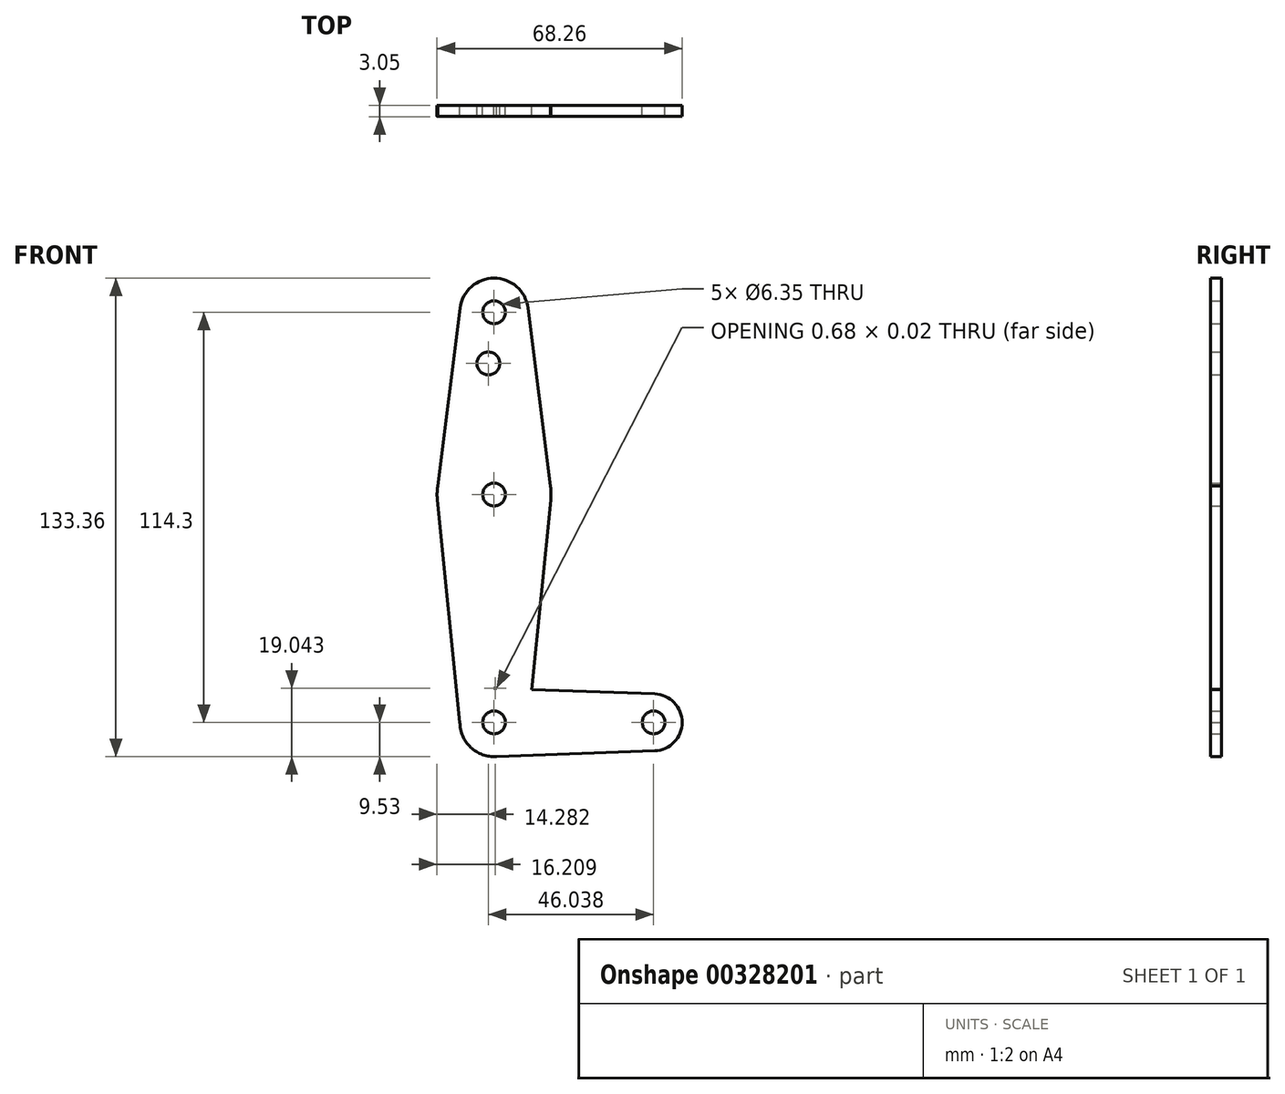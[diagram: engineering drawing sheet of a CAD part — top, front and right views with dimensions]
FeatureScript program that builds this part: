
annotation { "Feature Type Name" : "Feature", "Feature Type Description" : "" }
export const myFeature = defineFeature(function(context is Context, id is Id, definition is map)
    precondition{}
    {
        {
            var Q0;
            Q0=qCreatedBy(makeId("Front.planeOp"),FACE);
            var sketch = newSketch(context, id + "F0", { "sketchPlane" : qUnion([Q0])});
            skLineSegment(sketch, "E0", {"start": v(0, 0) * mm, "end": v(0, 114.3) * mm, "construction": true});
            skLineSegment(sketch, "E1", {"start": v(0, 0) * mm, "end": v(44.45, 0) * mm, "construction": true});
            skCircle(sketch, "E2", {"center": v(0, 114.3) * mm, "radius": 9.53 * mm});
            skCircle(sketch, "E3", {"center": v(0, 63.5) * mm, "radius": 15.88 * mm});
            skCircle(sketch, "E4", {"center": v(0, 0) * mm, "radius": 9.53 * mm});
            skCircle(sketch, "E5", {"center": v(44.45, 0) * mm, "radius": 7.94 * mm});
            skLineSegment(sketch, "E6", {"start": v(-9.53, 0) * mm, "end": v(-15.8, 61.9) * mm});
            skLineSegment(sketch, "E7", {"start": v(9.52, 0) * mm, "end": v(15.8, 61.9) * mm});
            skLineSegment(sketch, "E8", {"start": v(0, 9.53) * mm, "end": v(44.73, 7.93) * mm});
            skLineSegment(sketch, "E9", {"start": v(0, -9.53) * mm, "end": v(44.73, -7.93) * mm});
            skLineSegment(sketch, "E10", {"start": v(-15.8, 65.1) * mm, "end": v(-9.45, 115.49) * mm});
            skLineSegment(sketch, "E11", {"start": v(9.45, 115.49) * mm, "end": v(15.8, 65.1) * mm});
            skCircle(sketch, "E12", {"center": v(0, 114.3) * mm, "radius": 3.18 * mm});
            skCircle(sketch, "E13", {"center": v(-1.59, 100.03) * mm, "radius": 3.18 * mm});
            skCircle(sketch, "E14", {"center": v(0, 0) * mm, "radius": 3.18 * mm});
            skCircle(sketch, "E15", {"center": v(44.45, 0) * mm, "radius": 3.18 * mm});
            skCircle(sketch, "E16", {"center": v(0, 63.5) * mm, "radius": 3.18 * mm});
            skSolve(sketch);
        }
        {
            var Q0;
            Q0 = qSketchRegion(id + "F0", true);
            extrude(context, id + "F1", {"entities" : qUnion([Q0]), "depth" : 3.05 * mm});
        }
    });
